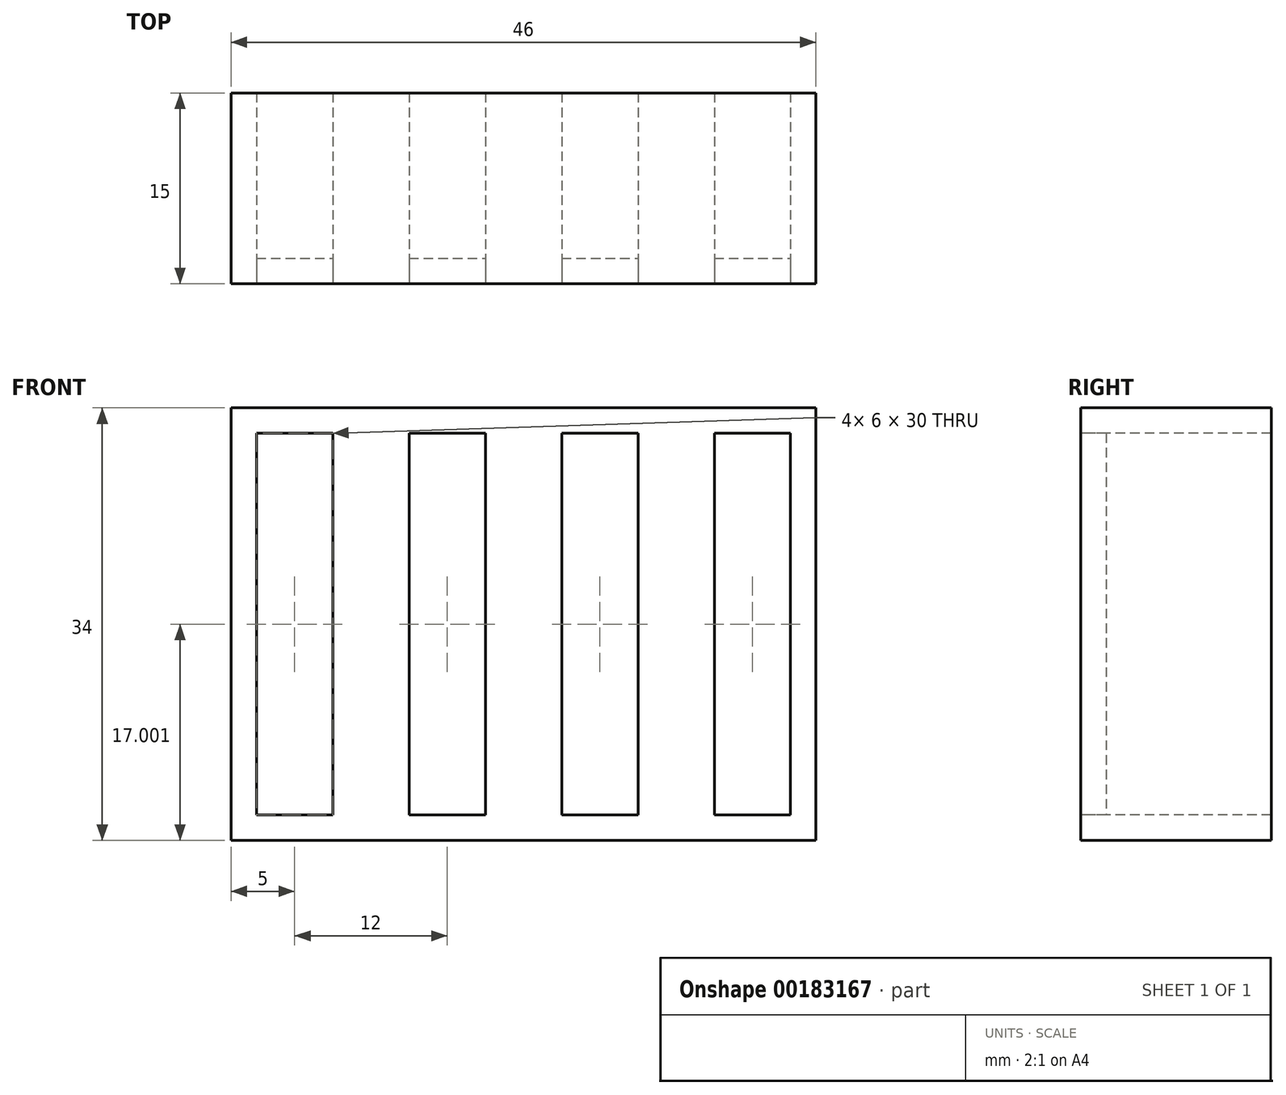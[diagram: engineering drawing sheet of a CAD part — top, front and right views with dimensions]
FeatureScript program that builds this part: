
annotation { "Feature Type Name" : "Feature", "Feature Type Description" : "" }
export const myFeature = defineFeature(function(context is Context, id is Id, definition is map)
    precondition{}
    {
        {
            var Q0;
            Q0=qCreatedBy(makeId("Front.planeOp"),FACE);
            var sketch = newSketch(context, id + "F0", { "sketchPlane" : qUnion([Q0])});
            skLineSegment(sketch, "E0.bottom", {"start": v(-141.27, 57.61) * mm, "end": v(-95.27, 57.61) * mm});
            skLineSegment(sketch, "E0.top", {"start": v(-141.27, 23.61) * mm, "end": v(-95.27, 23.61) * mm});
            skLineSegment(sketch, "E0.left", {"start": v(-141.27, 57.61) * mm, "end": v(-141.27, 23.61) * mm});
            skLineSegment(sketch, "E0.right", {"start": v(-95.27, 57.61) * mm, "end": v(-95.27, 23.61) * mm});
            skLineSegment(sketch, "E1.bottom", {"start": v(-139.27, 55.61) * mm, "end": v(-133.27, 55.61) * mm});
            skLineSegment(sketch, "E1.top", {"start": v(-139.27, 25.61) * mm, "end": v(-133.27, 25.61) * mm});
            skLineSegment(sketch, "E1.left", {"start": v(-139.27, 55.61) * mm, "end": v(-139.27, 25.61) * mm});
            skLineSegment(sketch, "E1.right", {"start": v(-133.27, 55.61) * mm, "end": v(-133.27, 25.61) * mm});
            skLineSegment(sketch, "E2.1.0.0", {"start": v(-121.27, 55.61) * mm, "end": v(-121.27, 25.61) * mm});
            skLineSegment(sketch, "E2.1.0.1", {"start": v(-127.27, 25.61) * mm, "end": v(-121.27, 25.61) * mm});
            skLineSegment(sketch, "E2.1.0.2", {"start": v(-127.27, 55.61) * mm, "end": v(-127.27, 25.61) * mm});
            skLineSegment(sketch, "E2.1.0.3", {"start": v(-127.27, 55.61) * mm, "end": v(-121.27, 55.61) * mm});
            skLineSegment(sketch, "E2.2.0.0", {"start": v(-109.27, 55.61) * mm, "end": v(-109.27, 25.61) * mm});
            skLineSegment(sketch, "E2.2.0.1", {"start": v(-115.27, 25.61) * mm, "end": v(-109.27, 25.61) * mm});
            skLineSegment(sketch, "E2.2.0.2", {"start": v(-115.27, 55.61) * mm, "end": v(-115.27, 25.61) * mm});
            skLineSegment(sketch, "E2.2.0.3", {"start": v(-115.27, 55.61) * mm, "end": v(-109.27, 55.61) * mm});
            skLineSegment(sketch, "E2.3.0.0", {"start": v(-97.27, 55.61) * mm, "end": v(-97.27, 25.61) * mm});
            skLineSegment(sketch, "E2.3.0.1", {"start": v(-103.27, 25.61) * mm, "end": v(-97.27, 25.61) * mm});
            skLineSegment(sketch, "E2.3.0.2", {"start": v(-103.27, 55.61) * mm, "end": v(-103.27, 25.61) * mm});
            skLineSegment(sketch, "E2.3.0.3", {"start": v(-103.27, 55.61) * mm, "end": v(-97.27, 55.61) * mm});
            skLineSegment(sketch, "E2.direction1", {"start": v(-133.27, 25.61) * mm, "end": v(-121.27, 25.61) * mm, "construction": true});
            skSolve(sketch);
        }
        {
            var Q0;
            Q0=makeQuery(id+"F0.imprint","IMPRINT",FACE,{"disambiguationData":[TD([[makeQuery(id+"F0.imprint","IMPRINT",EDGE,{"derivedFrom":sQuery(id+"F0.wireOp",EDGE,"E1.bottom")}),-1.0]])]});
            var Q1;
            Q1=makeQuery(id+"F0.imprint","IMPRINT",FACE,{"disambiguationData":[TD([[makeQuery(id+"F0.imprint","IMPRINT",EDGE,{"derivedFrom":sQuery(id+"F0.wireOp",EDGE,"E2.1.0.0")}),-1.0]])]});
            var Q2;
            Q2=makeQuery(id+"F0.imprint","IMPRINT",FACE,{"disambiguationData":[TD([[makeQuery(id+"F0.imprint","IMPRINT",EDGE,{"derivedFrom":sQuery(id+"F0.wireOp",EDGE,"E2.2.0.0")}),-1.0]])]});
            var Q3;
            Q3=makeQuery(id+"F0.imprint","IMPRINT",FACE,{"disambiguationData":[TD([[makeQuery(id+"F0.imprint","IMPRINT",EDGE,{"derivedFrom":sQuery(id+"F0.wireOp",EDGE,"E2.3.0.0")}),-1.0]])]});
            extrude(context, id + "F1", {"entities" : qUnion([Q0, Q1, Q2, Q3]), "oppositeDirection" : true, "depth" : 2 * mm});
        }
        {
            var Q0;
            Q0 = qSketchRegion(id + "F0", true);
            extrude(context, id + "F2", {"entities" : qUnion([Q0]), "oppositeDirection" : true, "depth" : 15 * mm});
        }
    });
